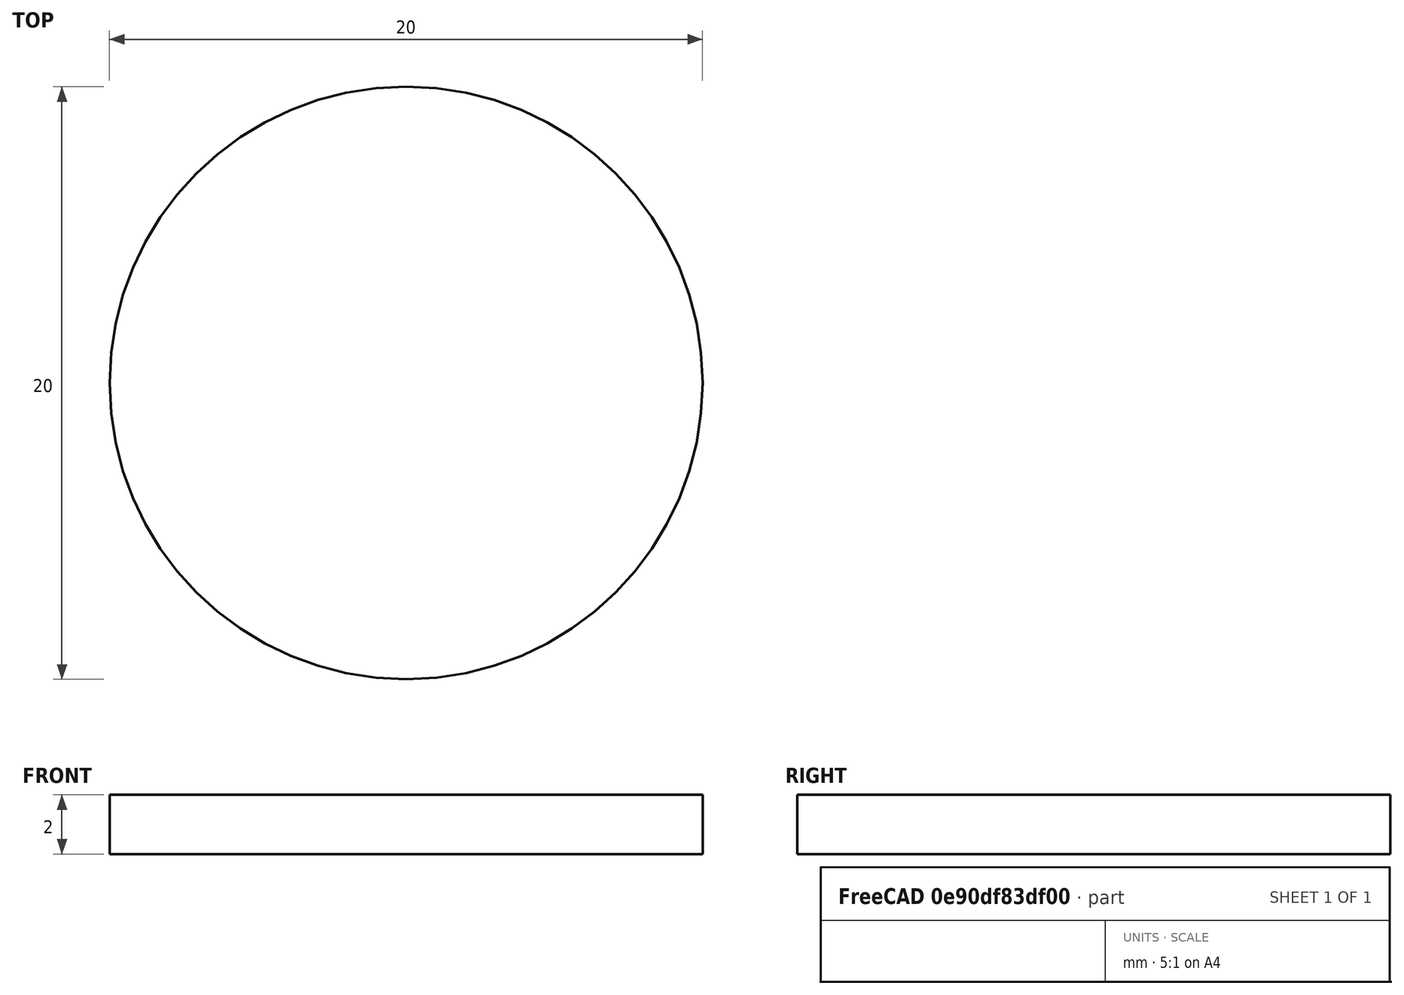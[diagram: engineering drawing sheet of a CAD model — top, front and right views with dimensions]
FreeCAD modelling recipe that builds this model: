
FCSTD DOCUMENT  (FreeCAD 0.19R24291 (Git))
Label: monets
License: All rights reserved
LicenseURL: http://en.wikipedia.org/wiki/All_rights_reserved
objects: Sketcher::SketchObject×2, PartDesign::Pad×1, PartDesign::Body×1
note: 5 computed .brp shape members not serialized (recipe doc carries the construction recipe); baked Part::Feature solids carry a one-line shape summary decoded from their .brp

FEATURE [Sketcher::SketchObject] Sketch
  FullyConstrained = false
  MapMode = 5
  Support = -> [XY_Plane]
  sketch-geometry (1):
    g0: Circle CenterX=-20.6061 CenterY=17.2727 CenterZ=0 NormalX=0 NormalY=0 NormalZ=1 AngleXU=0 Radius=10
  constraints (1):
    c: Radius(g0) = 10
FEATURE [PartDesign::Pad] Pad
  Direction = (1,1,1)
  Length = 2
  Length2 = 100
  Profile = -> Sketch
  Type = 0
FEATURE [Sketcher::SketchObject] Sketch001
  FullyConstrained = false
  MapMode = 5
  Placement = pos=(0,0,2) rot=(0,0,1;0rad)
  Support = -> [Pad]
  sketch-geometry (7):
    g0: LineSegment StartX=-26.4979 StartY=18.7718 StartZ=0 EndX=-21.7223 EndY=23.1252 EndZ=0
    g1: LineSegment StartX=-20.0125 StartY=24.2547 StartZ=0 EndX=-20.0125 EndY=10.8259 EndZ=0
    g2: LineSegment StartX=-20.0125 StartY=10.8259 StartZ=0 EndX=-21.7223 EndY=10.451 EndZ=0
    g3: LineSegment StartX=-21.7223 StartY=10.451 StartZ=0 EndX=-21.7223 EndY=23.1252 EndZ=0
    g4: LineSegment StartX=-21.7967 StartY=24.2547 StartZ=0 EndX=-20.0125 EndY=24.2547 EndZ=0
    g5: LineSegment StartX=-21.7967 StartY=24.2547 StartZ=0 EndX=-26.914 EndY=19.6623 EndZ=0
    g6: LineSegment StartX=-26.914 StartY=19.6623 StartZ=0 EndX=-26.4979 EndY=18.7718 EndZ=0
  constraints (10):
    c: Vertical(g1)
    c: Coincident(g2,g1)
    c: Vertical(g3)
    c: Coincident(g4,g1)
    c: Horizontal(g4)
    c: Coincident(g6,g0)
    c: Coincident(g0,g3)
    c: Coincident(g2,g3)
    c: Coincident(g5,g6)
    c: Coincident(g5,g4)
FEATURE [PartDesign::Body] Body
  Group = -> [Sketch,Pad,Sketch001]
  Origin = -> Origin
  Tip = -> Pad
